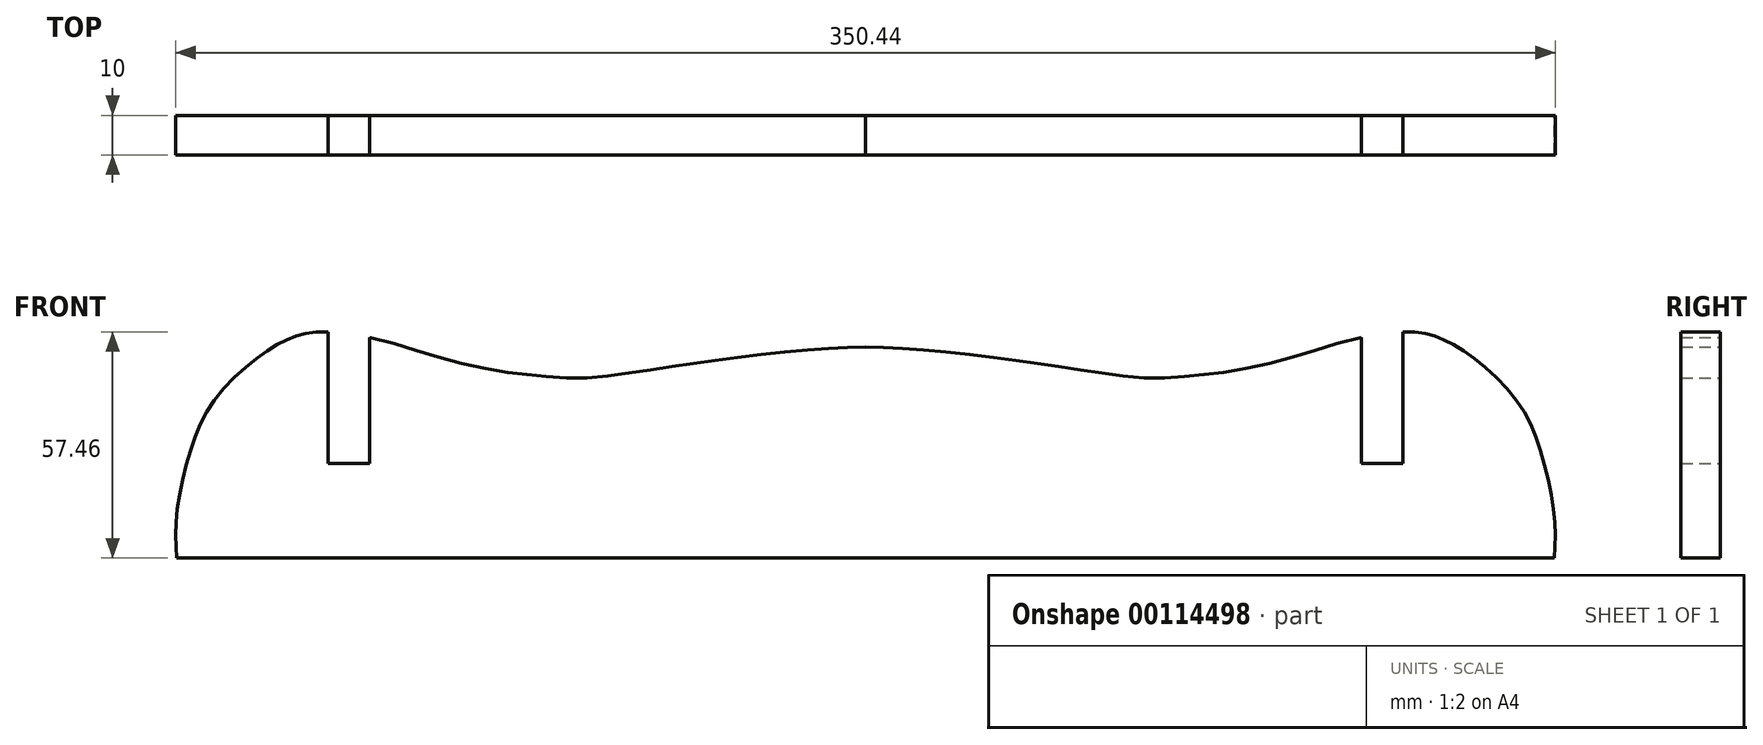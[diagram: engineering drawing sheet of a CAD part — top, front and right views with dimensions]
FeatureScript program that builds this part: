
annotation { "Feature Type Name" : "Feature", "Feature Type Description" : "" }
export const myFeature = defineFeature(function(context is Context, id is Id, definition is map)
    precondition{}
    {
        {
            var Q0;
            Q0=qCreatedBy(makeId("Front.planeOp"),FACE);
            var sketch = newSketch(context, id + "F0", { "sketchPlane" : qUnion([Q0])});
            skLineSegment(sketch, "E0", {"start": v(0, 0) * mm, "end": v(0, 240.25) * mm, "construction": true});
            skLineSegment(sketch, "E1", {"start": v(-175, 0) * mm, "end": v(175, 0) * mm});
            skLineSegment(sketch, "E2.bottom", {"start": v(126, 69) * mm, "end": v(136.5, 69) * mm});
            skLineSegment(sketch, "E2.top", {"start": v(126, 24) * mm, "end": v(136.5, 24) * mm});
            skLineSegment(sketch, "E2.left", {"start": v(126, 69) * mm, "end": v(126, 24) * mm});
            skLineSegment(sketch, "E2.right", {"start": v(136.5, 69) * mm, "end": v(136.5, 24) * mm});
            skFitSpline(sketch, "E3", {"points": [v(175, 0) * mm, v(175, 10.7) * mm, v(171.65, 26.7) * mm, v(165.64, 39.8) * mm, v(154.09, 51.15) * mm, v(145.74, 56) * mm, v(137.98, 57.46) * mm, v(121.78, 55.03) * mm, v(108.3, 50.96) * mm, v(93.35, 47.56) * mm, v(83.06, 46.3) * mm, v(72.2, 45.72) * mm, v(60.85, 46.88) * mm, v(48.33, 48.73) * mm, v(36.1, 50.47) * mm, v(21.45, 52.32) * mm, v(8.84, 53.29) * mm, v(0, 53.58) * mm], "startDerivative": vector(10.4, 184.82) * mm, "endDerivative": vector(-171.59, 4.09) * mm});
            skFitSpline(sketch, "E4.MirrorCS", {"points": [v(-175, 0) * mm, v(-175, 10.7) * mm, v(-171.65, 26.7) * mm, v(-165.64, 39.8) * mm, v(-154.09, 51.15) * mm, v(-145.74, 56) * mm, v(-137.98, 57.46) * mm, v(-121.78, 55.03) * mm, v(-108.3, 50.96) * mm, v(-93.35, 47.56) * mm, v(-83.06, 46.3) * mm, v(-72.2, 45.72) * mm, v(-60.85, 46.88) * mm, v(-48.33, 48.73) * mm, v(-36.1, 50.47) * mm, v(-21.45, 52.32) * mm, v(-8.84, 53.29) * mm, v(0, 53.58) * mm], "startDerivative": vector(-10.4, 184.82) * mm, "endDerivative": vector(171.59, 4.09) * mm});
            skLineSegment(sketch, "E5.MirrorCS", {"start": v(-126, 69) * mm, "end": v(-126, 24) * mm});
            skLineSegment(sketch, "E6.MirrorCS", {"start": v(-126, 69) * mm, "end": v(-136.5, 69) * mm});
            skLineSegment(sketch, "E7.MirrorCS", {"start": v(-136.5, 69) * mm, "end": v(-136.5, 24) * mm});
            skLineSegment(sketch, "E8.MirrorCS", {"start": v(-126, 24) * mm, "end": v(-136.5, 24) * mm});
            skSolve(sketch);
        }
        {
            var Q0;
            {var subQ5=sQuery(id+"F0.wireOp",EDGE,"E1");Q0=makeQuery(id+"F0.imprint","IMPRINT",FACE,{"disambiguationData":[TD([[makeQuery(id+"F0.imprint","IMPRINT",EDGE,{"derivedFrom":subQ5}),1.0]])]});}
            extrude(context, id + "F1", {"entities" : qUnion([Q0]), "endBound" : BoundingType.SYMMETRIC, "depth" : 10 * mm});
        }
    });
